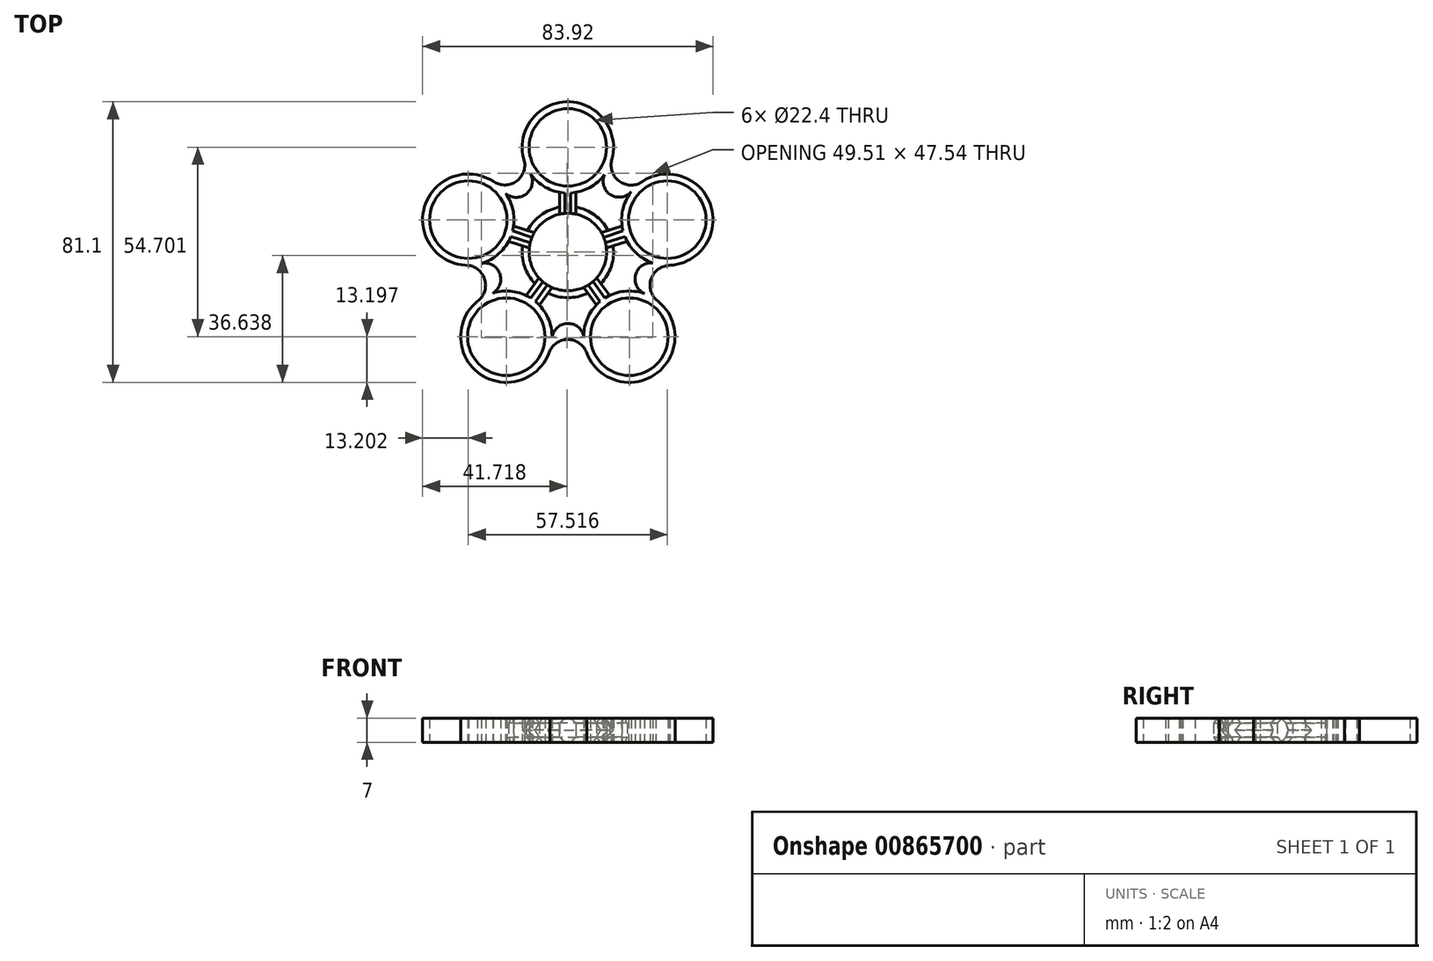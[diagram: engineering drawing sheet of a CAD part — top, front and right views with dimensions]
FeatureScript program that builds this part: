
annotation { "Feature Type Name" : "Feature", "Feature Type Description" : "" }
export const myFeature = defineFeature(function(context is Context, id is Id, definition is map)
    precondition{}
    {
        {
            var Q0;
            Q0=qCreatedBy(makeId("Top.planeOp"),FACE);
            var sketch = newSketch(context, id + "F0", { "sketchPlane" : qUnion([Q0])});
            skCircle(sketch, "E0", {"center": v(0, 0) * mm, "radius": 11.2 * mm});
            skCircle(sketch, "E1", {"center": v(0, 0) * mm, "radius": 13.2 * mm});
            skLineSegment(sketch, "E2", {"start": v(-2.34, 13) * mm, "end": v(-2.34, 18.14) * mm});
            skLineSegment(sketch, "E3", {"start": v(-2.34, 18.14) * mm, "end": v(2.33, 18.14) * mm});
            skLineSegment(sketch, "E4", {"start": v(2.33, 18.14) * mm, "end": v(2.33, 13) * mm});
            skCircle(sketch, "E5", {"center": v(0, 30.24) * mm, "radius": 13.2 * mm});
            skCircle(sketch, "E6", {"center": v(0, 30.24) * mm, "radius": 11.2 * mm});
            skCircle(sketch, "E7.1.0", {"center": v(-28.76, 9.34) * mm, "radius": 13.2 * mm});
            skCircle(sketch, "E7.1.1", {"center": v(-28.76, 9.34) * mm, "radius": 11.2 * mm});
            skLineSegment(sketch, "E7.1.2", {"start": v(-16.53, 7.82) * mm, "end": v(-11.64, 6.23) * mm});
            skLineSegment(sketch, "E7.1.3", {"start": v(-13.08, 1.78) * mm, "end": v(-17.98, 3.38) * mm});
            skLineSegment(sketch, "E7.1.4", {"start": v(-17.98, 3.38) * mm, "end": v(-16.53, 7.82) * mm});
            skCircle(sketch, "E7.2.0", {"center": v(-17.77, -24.46) * mm, "radius": 13.2 * mm});
            skCircle(sketch, "E7.2.1", {"center": v(-17.77, -24.46) * mm, "radius": 11.2 * mm});
            skLineSegment(sketch, "E7.2.2", {"start": v(-12.55, -13.3) * mm, "end": v(-9.52, -9.14) * mm});
            skLineSegment(sketch, "E7.2.3", {"start": v(-5.74, -11.89) * mm, "end": v(-8.77, -16.05) * mm});
            skLineSegment(sketch, "E7.2.4", {"start": v(-8.77, -16.05) * mm, "end": v(-12.55, -13.3) * mm});
            skCircle(sketch, "E7.3.0", {"center": v(17.77, -24.46) * mm, "radius": 13.2 * mm});
            skCircle(sketch, "E7.3.1", {"center": v(17.77, -24.46) * mm, "radius": 11.2 * mm});
            skLineSegment(sketch, "E7.3.2", {"start": v(8.78, -16.05) * mm, "end": v(5.75, -11.88) * mm});
            skLineSegment(sketch, "E7.3.3", {"start": v(9.53, -9.13) * mm, "end": v(12.56, -13.3) * mm});
            skLineSegment(sketch, "E7.3.4", {"start": v(12.56, -13.3) * mm, "end": v(8.78, -16.05) * mm});
            skCircle(sketch, "E7.4.0", {"center": v(28.76, 9.34) * mm, "radius": 13.2 * mm});
            skCircle(sketch, "E7.4.1", {"center": v(28.76, 9.34) * mm, "radius": 11.2 * mm});
            skLineSegment(sketch, "E7.4.2", {"start": v(17.97, 3.39) * mm, "end": v(13.08, 1.8) * mm});
            skLineSegment(sketch, "E7.4.3", {"start": v(11.63, 6.24) * mm, "end": v(16.53, 7.83) * mm});
            skLineSegment(sketch, "E7.4.4", {"start": v(16.53, 7.83) * mm, "end": v(17.97, 3.39) * mm});
            skArc(sketch, "E8", {"start": v(-17.98, 16.96) * mm, "mid": v(-11.96, 16.83) * mm, "end": v(-10.87, 22.75) * mm});
            skArc(sketch, "E9", {"start": v(-21.6, 20.43) * mm, "mid": v(-15.2, 20.23) * mm, "end": v(-12.5, 26.02) * mm});
            skArc(sketch, "E10.1.0", {"start": v(-26.1, -14.22) * mm, "mid": v(-23.93, -8.2) * mm, "end": v(-28.62, -3.86) * mm});
            skArc(sketch, "E10.1.1", {"start": v(-21.68, -11.86) * mm, "mid": v(-19.7, -6.17) * mm, "end": v(-25, -3.3) * mm});
            skArc(sketch, "E10.2.0", {"start": v(5.46, -29.22) * mm, "mid": v(0.41, -25.3) * mm, "end": v(-5.18, -28.4) * mm});
            skArc(sketch, "E10.2.1", {"start": v(4.57, -24.29) * mm, "mid": v(-0.22, -20.65) * mm, "end": v(-4.58, -24.8) * mm});
            skArc(sketch, "E10.3.0", {"start": v(29.48, -3.84) * mm, "mid": v(24.19, -7.43) * mm, "end": v(25.42, -13.7) * mm});
            skArc(sketch, "E10.3.1", {"start": v(24.51, -3.15) * mm, "mid": v(19.57, -6.59) * mm, "end": v(22.17, -12.02) * mm});
            skArc(sketch, "E10.4.0", {"start": v(12.76, 26.85) * mm, "mid": v(14.54, 20.7) * mm, "end": v(20.88, 19.94) * mm});
            skArc(sketch, "E10.4.1", {"start": v(10.57, 22.34) * mm, "mid": v(12.31, 16.58) * mm, "end": v(18.28, 17.37) * mm});
            skSolve(sketch);
        }
        {
            var Q0;
            {var subQ0=sQuery(id+"F0.wireOp",EDGE,"E8");Q0=makeQuery(id+"F0.imprint","IMPRINT",FACE,{"disambiguationData":[TD([[makeQuery(id+"F0.imprint","IMPRINT",EDGE,{"derivedFrom":subQ0}),1.0]])]});}
            var Q1;
            Q1=makeQuery(id+"F0.imprint","IMPRINT",FACE,{"disambiguationData":[TD([[makeQuery(id+"F0.imprint","IMPRINT",EDGE,{"derivedFrom":sQuery(id+"F0.wireOp",EDGE,"E7.1.1")}),-1.0]])]});
            var Q2;
            {var subQ5=sQuery(id+"F0.wireOp",EDGE,"E7.1.4");Q2=makeQuery(id+"F0.imprint","IMPRINT",FACE,{"disambiguationData":[TD([[makeQuery(id+"F0.imprint","IMPRINT",EDGE,{"derivedFrom":subQ5}),-1.0]])]});}
            var Q3;
            {var subQ0=sQuery(id+"F0.wireOp",EDGE,"E7.1.2");var subQ1=sQuery(id+"F0.wireOp",EDGE,"E1");var subQ2=makeQuery(id+"F0.imprint","INTERSECT",VERTEX,{"derivedFrom":[subQ1,subQ0]});Q3=makeQuery(id+"F0.imprint","IMPRINT",FACE,{"disambiguationData":[TD([[makeQuery(id+"F0.imprint","IMPRINT",EDGE,{"disambiguationData":[TD([[subQ2,-1.0]])],"derivedFrom":subQ1}),-1.0]])]});}
            var Q4;
            {var subQ0=sQuery(id+"F0.wireOp",EDGE,"E3");Q4=makeQuery(id+"F0.imprint","IMPRINT",FACE,{"disambiguationData":[TD([[makeQuery(id+"F0.imprint","IMPRINT",EDGE,{"derivedFrom":subQ0}),-1.0]])]});}
            var Q5;
            {var subQ4=sQuery(id+"F0.wireOp",EDGE,"E3");Q5=makeQuery(id+"F0.imprint","IMPRINT",FACE,{"disambiguationData":[TD([[makeQuery(id+"F0.imprint","IMPRINT",EDGE,{"derivedFrom":subQ4}),1.0]])]});}
            var Q6;
            {var subQ0=sQuery(id+"F0.wireOp",EDGE,"E10.4.1");Q6=makeQuery(id+"F0.imprint","IMPRINT",FACE,{"disambiguationData":[TD([[makeQuery(id+"F0.imprint","IMPRINT",EDGE,{"derivedFrom":subQ0}),1.0]])]});}
            var Q7;
            {var subQ5=sQuery(id+"F0.wireOp",EDGE,"E7.4.4");Q7=makeQuery(id+"F0.imprint","IMPRINT",FACE,{"disambiguationData":[TD([[makeQuery(id+"F0.imprint","IMPRINT",EDGE,{"derivedFrom":subQ5}),-1.0]])]});}
            var Q8;
            {var subQ5=sQuery(id+"F0.wireOp",EDGE,"E7.3.4");Q8=makeQuery(id+"F0.imprint","IMPRINT",FACE,{"disambiguationData":[TD([[makeQuery(id+"F0.imprint","IMPRINT",EDGE,{"derivedFrom":subQ5}),-1.0]])]});}
            var Q9;
            {var subQ5=sQuery(id+"F0.wireOp",EDGE,"E7.2.4");Q9=makeQuery(id+"F0.imprint","IMPRINT",FACE,{"disambiguationData":[TD([[makeQuery(id+"F0.imprint","IMPRINT",EDGE,{"derivedFrom":subQ5}),-1.0]])]});}
            var Q10;
            {var subQ0=sQuery(id+"F0.wireOp",EDGE,"E7.2.2");var subQ1=sQuery(id+"F0.wireOp",EDGE,"E1");var subQ2=makeQuery(id+"F0.imprint","INTERSECT",VERTEX,{"derivedFrom":[subQ1,subQ0]});Q10=makeQuery(id+"F0.imprint","IMPRINT",FACE,{"disambiguationData":[TD([[makeQuery(id+"F0.imprint","IMPRINT",EDGE,{"disambiguationData":[TD([[subQ2,-1.0]])],"derivedFrom":subQ1}),-1.0]])]});}
            var Q11;
            Q11=makeQuery(id+"F0.imprint","IMPRINT",FACE,{"disambiguationData":[TD([[makeQuery(id+"F0.imprint","IMPRINT",EDGE,{"derivedFrom":sQuery(id+"F0.wireOp",EDGE,"E0")}),-1.0]])]});
            var Q12;
            {var subQ0=sQuery(id+"F0.wireOp",EDGE,"E7.4.2");var subQ1=sQuery(id+"F0.wireOp",EDGE,"E1");var subQ2=makeQuery(id+"F0.imprint","INTERSECT",VERTEX,{"derivedFrom":[subQ1,subQ0]});Q12=makeQuery(id+"F0.imprint","IMPRINT",FACE,{"disambiguationData":[TD([[makeQuery(id+"F0.imprint","IMPRINT",EDGE,{"disambiguationData":[TD([[subQ2,-1.0]])],"derivedFrom":subQ1}),-1.0]])]});}
            var Q13;
            {var subQ0=sQuery(id+"F0.wireOp",EDGE,"E2");var subQ1=sQuery(id+"F0.wireOp",EDGE,"E1");var subQ2=makeQuery(id+"F0.imprint","INTERSECT",VERTEX,{"derivedFrom":[subQ1,subQ0]});Q13=makeQuery(id+"F0.imprint","IMPRINT",FACE,{"disambiguationData":[TD([[makeQuery(id+"F0.imprint","IMPRINT",EDGE,{"disambiguationData":[TD([[subQ2,1.0]])],"derivedFrom":subQ1}),-1.0]])]});}
            var Q14;
            {var subQ0=sQuery(id+"F0.wireOp",EDGE,"E7.3.2");var subQ1=sQuery(id+"F0.wireOp",EDGE,"E1");var subQ2=makeQuery(id+"F0.imprint","INTERSECT",VERTEX,{"derivedFrom":[subQ1,subQ0]});Q14=makeQuery(id+"F0.imprint","IMPRINT",FACE,{"disambiguationData":[TD([[makeQuery(id+"F0.imprint","IMPRINT",EDGE,{"disambiguationData":[TD([[subQ2,-1.0]])],"derivedFrom":subQ1}),-1.0]])]});}
            var Q15;
            Q15=makeQuery(id+"F0.imprint","IMPRINT",FACE,{"disambiguationData":[TD([[makeQuery(id+"F0.imprint","IMPRINT",EDGE,{"derivedFrom":sQuery(id+"F0.wireOp",EDGE,"E7.3.1")}),-1.0]])]});
            var Q16;
            {var subQ3=sQuery(id+"F0.wireOp",EDGE,"E10.2.1");Q16=makeQuery(id+"F0.imprint","IMPRINT",FACE,{"disambiguationData":[TD([[makeQuery(id+"F0.imprint","IMPRINT",EDGE,{"derivedFrom":subQ3}),1.0]])]});}
            var Q17;
            Q17=makeQuery(id+"F0.imprint","IMPRINT",FACE,{"disambiguationData":[TD([[makeQuery(id+"F0.imprint","IMPRINT",EDGE,{"derivedFrom":sQuery(id+"F0.wireOp",EDGE,"E7.2.1")}),-1.0]])]});
            var Q18;
            {var subQ3=sQuery(id+"F0.wireOp",EDGE,"E10.1.1");Q18=makeQuery(id+"F0.imprint","IMPRINT",FACE,{"disambiguationData":[TD([[makeQuery(id+"F0.imprint","IMPRINT",EDGE,{"derivedFrom":subQ3}),1.0]])]});}
            var Q19;
            Q19=makeQuery(id+"F0.imprint","IMPRINT",FACE,{"disambiguationData":[TD([[makeQuery(id+"F0.imprint","IMPRINT",EDGE,{"derivedFrom":sQuery(id+"F0.wireOp",EDGE,"E7.4.1")}),-1.0]])]});
            var Q20;
            {var subQ3=sQuery(id+"F0.wireOp",EDGE,"E10.3.1");Q20=makeQuery(id+"F0.imprint","IMPRINT",FACE,{"disambiguationData":[TD([[makeQuery(id+"F0.imprint","IMPRINT",EDGE,{"derivedFrom":subQ3}),1.0]])]});}
            extrude(context, id + "F1", {"entities" : qUnion([Q0, Q1, Q2, Q3, Q4, Q5, Q6, Q7, Q8, Q9, Q10, Q11, Q12, Q13, Q14, Q15, Q16, Q17, Q18, Q19, Q20]), "depth" : 7 * mm, "offsetDistance" : 25 * mm});
        }
        {
            var Q0;
            {var subQ0=sQuery(id+"F0.wireOp",EDGE,"E1");Q0=makeQuery(id+"F1.opExtrude","CAP_EDGE",EDGE,{"disambiguationData":[OSD([subQ0]),TDD([makeQuery(id+"F0.imprint","IMPRINT",EDGE,{"disambiguationData":[TD([[makeQuery(id+"F0.imprint","INTERSECT",VERTEX,{"derivedFrom":[subQ0,sQuery(id+"F0.wireOp",EDGE,"E7.3.3")]}),-1.0]])],"derivedFrom":subQ0})])],"isStart":false});}
            var Q1;
            {var subQ0=sQuery(id+"F0.wireOp",EDGE,"E1");Q1=makeQuery(id+"F1.opExtrude","CAP_EDGE",EDGE,{"disambiguationData":[OSD([subQ0]),TDD([makeQuery(id+"F0.imprint","IMPRINT",EDGE,{"disambiguationData":[TD([[makeQuery(id+"F0.imprint","INTERSECT",VERTEX,{"derivedFrom":[subQ0,sQuery(id+"F0.wireOp",EDGE,"E4")]}),1.0]])],"derivedFrom":subQ0})])],"isStart":false});}
            var Q2;
            {var subQ0=sQuery(id+"F0.wireOp",EDGE,"E1");Q2=makeQuery(id+"F1.opExtrude","CAP_EDGE",EDGE,{"disambiguationData":[OSD([subQ0]),TDD([makeQuery(id+"F0.imprint","IMPRINT",EDGE,{"disambiguationData":[TD([[makeQuery(id+"F0.imprint","INTERSECT",VERTEX,{"derivedFrom":[subQ0,sQuery(id+"F0.wireOp",EDGE,"E2")]}),-1.0]])],"derivedFrom":subQ0})])],"isStart":false});}
            var Q3;
            {var subQ0=sQuery(id+"F0.wireOp",EDGE,"E1");Q3=makeQuery(id+"F1.opExtrude","CAP_EDGE",EDGE,{"disambiguationData":[OSD([subQ0]),TDD([makeQuery(id+"F0.imprint","IMPRINT",EDGE,{"disambiguationData":[TD([[makeQuery(id+"F0.imprint","INTERSECT",VERTEX,{"derivedFrom":[subQ0,sQuery(id+"F0.wireOp",EDGE,"E7.1.3")]}),-1.0]])],"derivedFrom":subQ0})])],"isStart":false});}
            var Q4;
            {var subQ0=sQuery(id+"F0.wireOp",EDGE,"E1");Q4=makeQuery(id+"F1.opExtrude","CAP_EDGE",EDGE,{"disambiguationData":[OSD([subQ0]),TDD([makeQuery(id+"F0.imprint","IMPRINT",EDGE,{"disambiguationData":[TD([[makeQuery(id+"F0.imprint","INTERSECT",VERTEX,{"derivedFrom":[subQ0,sQuery(id+"F0.wireOp",EDGE,"E7.2.3")]}),-1.0]])],"derivedFrom":subQ0})])],"isStart":false});}
            chamfer(context, id + "F2", {"entities" : qUnion([Q0, Q1, Q2, Q3, Q4]), "width" : 3.5 * mm, "tangentPropagation" : true});
        }
        {
            var Q0;
            {var subQ0=sQuery(id+"F0.wireOp",EDGE,"E1");Q0=makeQuery(id+"F1.opExtrude","CAP_EDGE",EDGE,{"disambiguationData":[OSD([subQ0]),TDD([makeQuery(id+"F0.imprint","IMPRINT",EDGE,{"disambiguationData":[TD([[makeQuery(id+"F0.imprint","INTERSECT",VERTEX,{"derivedFrom":[subQ0,sQuery(id+"F0.wireOp",EDGE,"E4")]}),1.0]])],"derivedFrom":subQ0})])],"isStart":true});}
            var Q1;
            {var subQ0=sQuery(id+"F0.wireOp",EDGE,"E1");Q1=makeQuery(id+"F1.opExtrude","CAP_EDGE",EDGE,{"disambiguationData":[OSD([subQ0]),TDD([makeQuery(id+"F0.imprint","IMPRINT",EDGE,{"disambiguationData":[TD([[makeQuery(id+"F0.imprint","INTERSECT",VERTEX,{"derivedFrom":[subQ0,sQuery(id+"F0.wireOp",EDGE,"E2")]}),-1.0]])],"derivedFrom":subQ0})])],"isStart":true});}
            var Q2;
            {var subQ0=sQuery(id+"F0.wireOp",EDGE,"E1");Q2=makeQuery(id+"F1.opExtrude","CAP_EDGE",EDGE,{"disambiguationData":[OSD([subQ0]),TDD([makeQuery(id+"F0.imprint","IMPRINT",EDGE,{"disambiguationData":[TD([[makeQuery(id+"F0.imprint","INTERSECT",VERTEX,{"derivedFrom":[subQ0,sQuery(id+"F0.wireOp",EDGE,"E7.1.3")]}),-1.0]])],"derivedFrom":subQ0})])],"isStart":true});}
            var Q3;
            {var subQ0=sQuery(id+"F0.wireOp",EDGE,"E1");Q3=makeQuery(id+"F1.opExtrude","CAP_EDGE",EDGE,{"disambiguationData":[OSD([subQ0]),TDD([makeQuery(id+"F0.imprint","IMPRINT",EDGE,{"disambiguationData":[TD([[makeQuery(id+"F0.imprint","INTERSECT",VERTEX,{"derivedFrom":[subQ0,sQuery(id+"F0.wireOp",EDGE,"E7.2.3")]}),-1.0]])],"derivedFrom":subQ0})])],"isStart":true});}
            var Q4;
            {var subQ0=sQuery(id+"F0.wireOp",EDGE,"E1");Q4=makeQuery(id+"F1.opExtrude","CAP_EDGE",EDGE,{"disambiguationData":[OSD([subQ0]),TDD([makeQuery(id+"F0.imprint","IMPRINT",EDGE,{"disambiguationData":[TD([[makeQuery(id+"F0.imprint","INTERSECT",VERTEX,{"derivedFrom":[subQ0,sQuery(id+"F0.wireOp",EDGE,"E7.3.3")]}),-1.0]])],"derivedFrom":subQ0})])],"isStart":true});}
            chamfer(context, id + "F3", {"entities" : qUnion([Q0, Q1, Q2, Q3, Q4]), "width" : 3.5 * mm, "tangentPropagation" : true});
        }
        {
            var Q0;
            Q0=makeQuery(id+"F1.opExtrude","CAP_EDGE",EDGE,{"disambiguationData":[OSD([sQuery(id+"F0.wireOp",EDGE,"E10.3.0")])],"isStart":true});
            var Q1;
            Q1=makeQuery(id+"F1.opExtrude","CAP_EDGE",EDGE,{"disambiguationData":[OSD([sQuery(id+"F0.wireOp",EDGE,"E10.4.0")])],"isStart":true});
            var Q2;
            Q2=makeQuery(id+"F1.opExtrude","CAP_EDGE",EDGE,{"disambiguationData":[OSD([sQuery(id+"F0.wireOp",EDGE,"E9")])],"isStart":true});
            var Q3;
            Q3=makeQuery(id+"F1.opExtrude","CAP_EDGE",EDGE,{"disambiguationData":[OSD([sQuery(id+"F0.wireOp",EDGE,"E10.1.0")])],"isStart":true});
            var Q4;
            Q4=makeQuery(id+"F1.opExtrude","CAP_EDGE",EDGE,{"disambiguationData":[OSD([sQuery(id+"F0.wireOp",EDGE,"E10.2.0")])],"isStart":true});
            fillet(context, id + "F4", {"entities" : qUnion([Q0, Q1, Q2, Q3, Q4]), "radius" : 0.02 * mm, "tangentPropagation" : true, "allowEdgeOverflow" : false});
        }
        {
            var Q0;
            Q0=makeQuery(id+"F1.opExtrude","CAP_EDGE",EDGE,{"disambiguationData":[OSD([sQuery(id+"F0.wireOp",EDGE,"E4")])],"isStart":true});
            var Q1;
            Q1=makeQuery(id+"F1.opExtrude","CAP_EDGE",EDGE,{"disambiguationData":[OSD([sQuery(id+"F0.wireOp",EDGE,"E2")])],"isStart":true});
            var Q2;
            Q2=makeQuery(id+"F1.opExtrude","CAP_EDGE",EDGE,{"disambiguationData":[OSD([sQuery(id+"F0.wireOp",EDGE,"E7.1.2")])],"isStart":true});
            var Q3;
            Q3=makeQuery(id+"F1.opExtrude","CAP_EDGE",EDGE,{"disambiguationData":[OSD([sQuery(id+"F0.wireOp",EDGE,"E7.1.3")])],"isStart":true});
            var Q4;
            Q4=makeQuery(id+"F1.opExtrude","CAP_EDGE",EDGE,{"disambiguationData":[OSD([sQuery(id+"F0.wireOp",EDGE,"E7.2.2")])],"isStart":true});
            var Q5;
            Q5=makeQuery(id+"F1.opExtrude","CAP_EDGE",EDGE,{"disambiguationData":[OSD([sQuery(id+"F0.wireOp",EDGE,"E7.2.3")])],"isStart":true});
            var Q6;
            Q6=makeQuery(id+"F1.opExtrude","CAP_EDGE",EDGE,{"disambiguationData":[OSD([sQuery(id+"F0.wireOp",EDGE,"E7.3.2")])],"isStart":true});
            var Q7;
            Q7=makeQuery(id+"F1.opExtrude","CAP_EDGE",EDGE,{"disambiguationData":[OSD([sQuery(id+"F0.wireOp",EDGE,"E7.3.3")])],"isStart":true});
            var Q8;
            Q8=makeQuery(id+"F1.opExtrude","CAP_EDGE",EDGE,{"disambiguationData":[OSD([sQuery(id+"F0.wireOp",EDGE,"E7.4.2")])],"isStart":true});
            var Q9;
            Q9=makeQuery(id+"F1.opExtrude","CAP_EDGE",EDGE,{"disambiguationData":[OSD([sQuery(id+"F0.wireOp",EDGE,"E7.4.3")])],"isStart":true});
            chamfer(context, id + "F5", {"entities" : qUnion([Q0, Q1, Q2, Q3, Q4, Q5, Q6, Q7, Q8, Q9]), "width" : 1.5 * mm, "tangentPropagation" : true});
        }
        {
            var Q0;
            Q0=makeQuery(id+"F1.opExtrude","CAP_EDGE",EDGE,{"disambiguationData":[OSD([sQuery(id+"F0.wireOp",EDGE,"E7.1.2")])],"isStart":false});
            var Q1;
            Q1=makeQuery(id+"F1.opExtrude","CAP_EDGE",EDGE,{"disambiguationData":[OSD([sQuery(id+"F0.wireOp",EDGE,"E7.1.3")])],"isStart":false});
            var Q2;
            Q2=makeQuery(id+"F1.opExtrude","CAP_EDGE",EDGE,{"disambiguationData":[OSD([sQuery(id+"F0.wireOp",EDGE,"E2")])],"isStart":false});
            var Q3;
            Q3=makeQuery(id+"F1.opExtrude","CAP_EDGE",EDGE,{"disambiguationData":[OSD([sQuery(id+"F0.wireOp",EDGE,"E4")])],"isStart":false});
            var Q4;
            Q4=makeQuery(id+"F1.opExtrude","CAP_EDGE",EDGE,{"disambiguationData":[OSD([sQuery(id+"F0.wireOp",EDGE,"E7.4.3")])],"isStart":false});
            var Q5;
            Q5=makeQuery(id+"F1.opExtrude","CAP_EDGE",EDGE,{"disambiguationData":[OSD([sQuery(id+"F0.wireOp",EDGE,"E7.4.2")])],"isStart":false});
            var Q6;
            Q6=makeQuery(id+"F1.opExtrude","CAP_EDGE",EDGE,{"disambiguationData":[OSD([sQuery(id+"F0.wireOp",EDGE,"E7.3.3")])],"isStart":false});
            var Q7;
            Q7=makeQuery(id+"F1.opExtrude","CAP_EDGE",EDGE,{"disambiguationData":[OSD([sQuery(id+"F0.wireOp",EDGE,"E7.3.2")])],"isStart":false});
            var Q8;
            Q8=makeQuery(id+"F1.opExtrude","CAP_EDGE",EDGE,{"disambiguationData":[OSD([sQuery(id+"F0.wireOp",EDGE,"E7.2.3")])],"isStart":false});
            var Q9;
            Q9=makeQuery(id+"F1.opExtrude","CAP_EDGE",EDGE,{"disambiguationData":[OSD([sQuery(id+"F0.wireOp",EDGE,"E7.2.2")])],"isStart":false});
            chamfer(context, id + "F6", {"entities" : qUnion([Q0, Q1, Q2, Q3, Q4, Q5, Q6, Q7, Q8, Q9]), "width" : 1.5 * mm, "tangentPropagation" : true});
        }
    });
